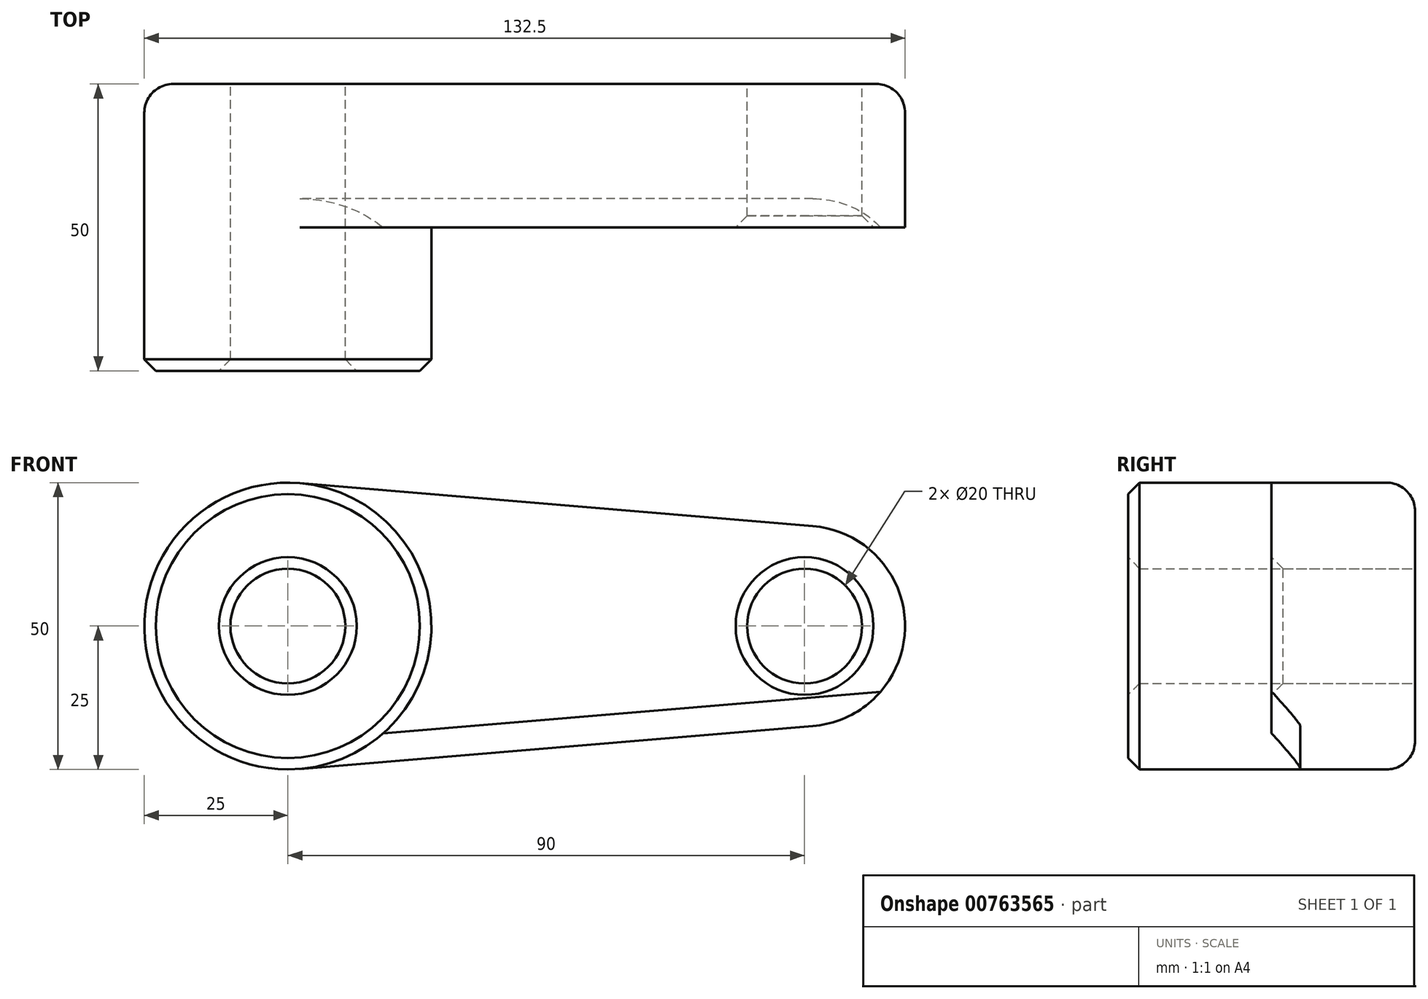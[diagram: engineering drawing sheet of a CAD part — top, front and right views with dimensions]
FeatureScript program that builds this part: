
annotation { "Feature Type Name" : "Feature", "Feature Type Description" : "" }
export const myFeature = defineFeature(function(context is Context, id is Id, definition is map)
    precondition{}
    {
        {
            var Q0;
            Q0=qCreatedBy(makeId("Front.planeOp"),FACE);
            var sketch = newSketch(context, id + "F0", { "sketchPlane" : qUnion([Q0])});
            skCircle(sketch, "E0", {"center": v(0, 0) * mm, "radius": 25 * mm});
            skCircle(sketch, "E1", {"center": v(90, 0) * mm, "radius": 17.5 * mm});
            skLineSegment(sketch, "E2", {"start": v(2.08, 24.91) * mm, "end": v(91.46, 17.44) * mm});
            skLineSegment(sketch, "E3", {"start": v(2.08, -24.91) * mm, "end": v(91.46, -17.44) * mm});
            skCircle(sketch, "E4", {"center": v(0, 0) * mm, "radius": 10 * mm});
            skCircle(sketch, "E5", {"center": v(90, 0) * mm, "radius": 10 * mm});
            skSolve(sketch);
        }
        {
            var Q0;
            Q0=qSketchRegion(id+"F0",true);
            extrude(context, id + "F1", {"entities" : qUnion([Q0]), "depth" : 25 * mm});
        }
        {
            var Q0;
            Q0=makeQuery(id+"F0.imprint","IMPRINT",FACE,{"disambiguationData":[TD([[makeQuery(id+"F0.imprint","IMPRINT",EDGE,{"derivedFrom":sQuery(id+"F0.wireOp",EDGE,"E4")}),-1.0]])]});
            extrude(context, id + "F2", {"entities" : qUnion([Q0]), "operationType" : NewBodyOperationType.ADD, "depth" : 50 * mm});
        }
        {
            var Q0;
            Q0=makeQuery(id+"F2.opExtrude","CAP_EDGE",EDGE,{"disambiguationData":[OSD([sQuery(id+"F0.wireOp",EDGE,"E0")])],"isStart":false});
            var Q1;
            Q1=makeQuery(id+"F2.opExtrude","CAP_EDGE",EDGE,{"disambiguationData":[OSD([sQuery(id+"F0.wireOp",EDGE,"E4")])],"isStart":false});
            var Q2;
            Q2=makeQuery(id+"F1.opExtrude","CAP_EDGE",EDGE,{"disambiguationData":[OSD([sQuery(id+"F0.wireOp",EDGE,"E5")])],"isStart":false});
            chamfer(context, id + "F3", {"entities" : qUnion([Q0, Q1, Q2]), "width" : 2 * mm, "tangentPropagation" : true});
        }
        {
            var Q0;
            Q0=makeQuery(id+"F1.opExtrude","CAP_EDGE",EDGE,{"disambiguationData":[OSD([sQuery(id+"F0.wireOp",EDGE,"E3")])],"isStart":true});
            fillet(context, id + "F4", {"entities" : qUnion([Q0]), "radius" : 5 * mm, "tangentPropagation" : true, "allowEdgeOverflow" : false});
        }
        {
            var Q0;
            Q0=makeQuery(id+"F1.opExtrude","CAP_EDGE",EDGE,{"disambiguationData":[OSD([sQuery(id+"F0.wireOp",EDGE,"E3")])],"isStart":false});
            chamfer(context, id + "F5", {"entities" : qUnion([Q0]), "width" : 5 * mm});
        }
    });
